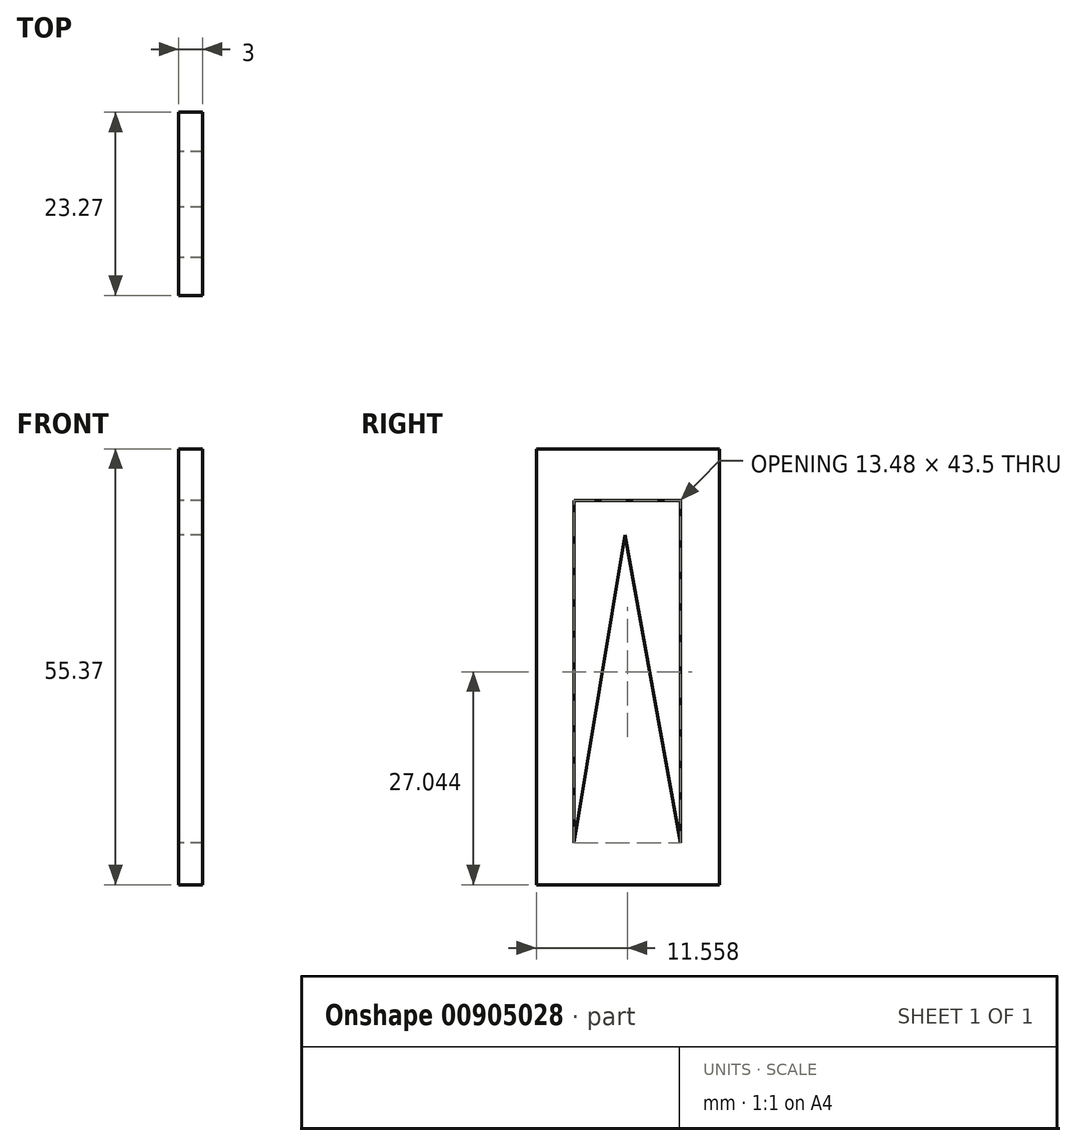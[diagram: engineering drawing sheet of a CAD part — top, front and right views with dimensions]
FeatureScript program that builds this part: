
annotation { "Feature Type Name" : "Feature", "Feature Type Description" : "" }
export const myFeature = defineFeature(function(context is Context, id is Id, definition is map)
    precondition{}
    {
        {
            var Q0;
            Q0=qCreatedBy(makeId("Right.planeOp"),FACE);
            var sketch = newSketch(context, id + "F0", { "sketchPlane" : qUnion([Q0])});
            skLineSegment(sketch, "E0", {"start": v(10.15, -12.08) * mm, "end": v(10.15, -67.45) * mm});
            skLineSegment(sketch, "E1", {"start": v(10.15, -67.45) * mm, "end": v(33.42, -67.45) * mm});
            skLineSegment(sketch, "E2", {"start": v(33.42, -67.45) * mm, "end": v(33.42, -12.08) * mm});
            skLineSegment(sketch, "E3", {"start": v(33.42, -12.08) * mm, "end": v(10.15, -12.08) * mm});
            skLineSegment(sketch, "E4", {"start": v(14.97, -18.66) * mm, "end": v(14.97, -62.15) * mm});
            skLineSegment(sketch, "E5", {"start": v(14.97, -62.15) * mm, "end": v(21.39, -23) * mm});
            skLineSegment(sketch, "E6", {"start": v(21.39, -23) * mm, "end": v(28.45, -62.15) * mm});
            skLineSegment(sketch, "E7", {"start": v(28.45, -62.15) * mm, "end": v(28.45, -18.66) * mm});
            skLineSegment(sketch, "E8", {"start": v(28.45, -18.66) * mm, "end": v(14.97, -18.66) * mm});
            skSolve(sketch);
        }
        {
            var Q0;
            Q0=makeQuery(id+"F0.imprint","IMPRINT",FACE,{"disambiguationData":[TD([[makeQuery(id+"F0.imprint","IMPRINT",EDGE,{"derivedFrom":sQuery(id+"F0.wireOp",EDGE,"E0")}),1.0]])]});
            extrude(context, id + "F1", {"entities" : qUnion([Q0]), "depth" : 3 * mm, "offsetDistance" : 25.4 * mm});
        }
    });
